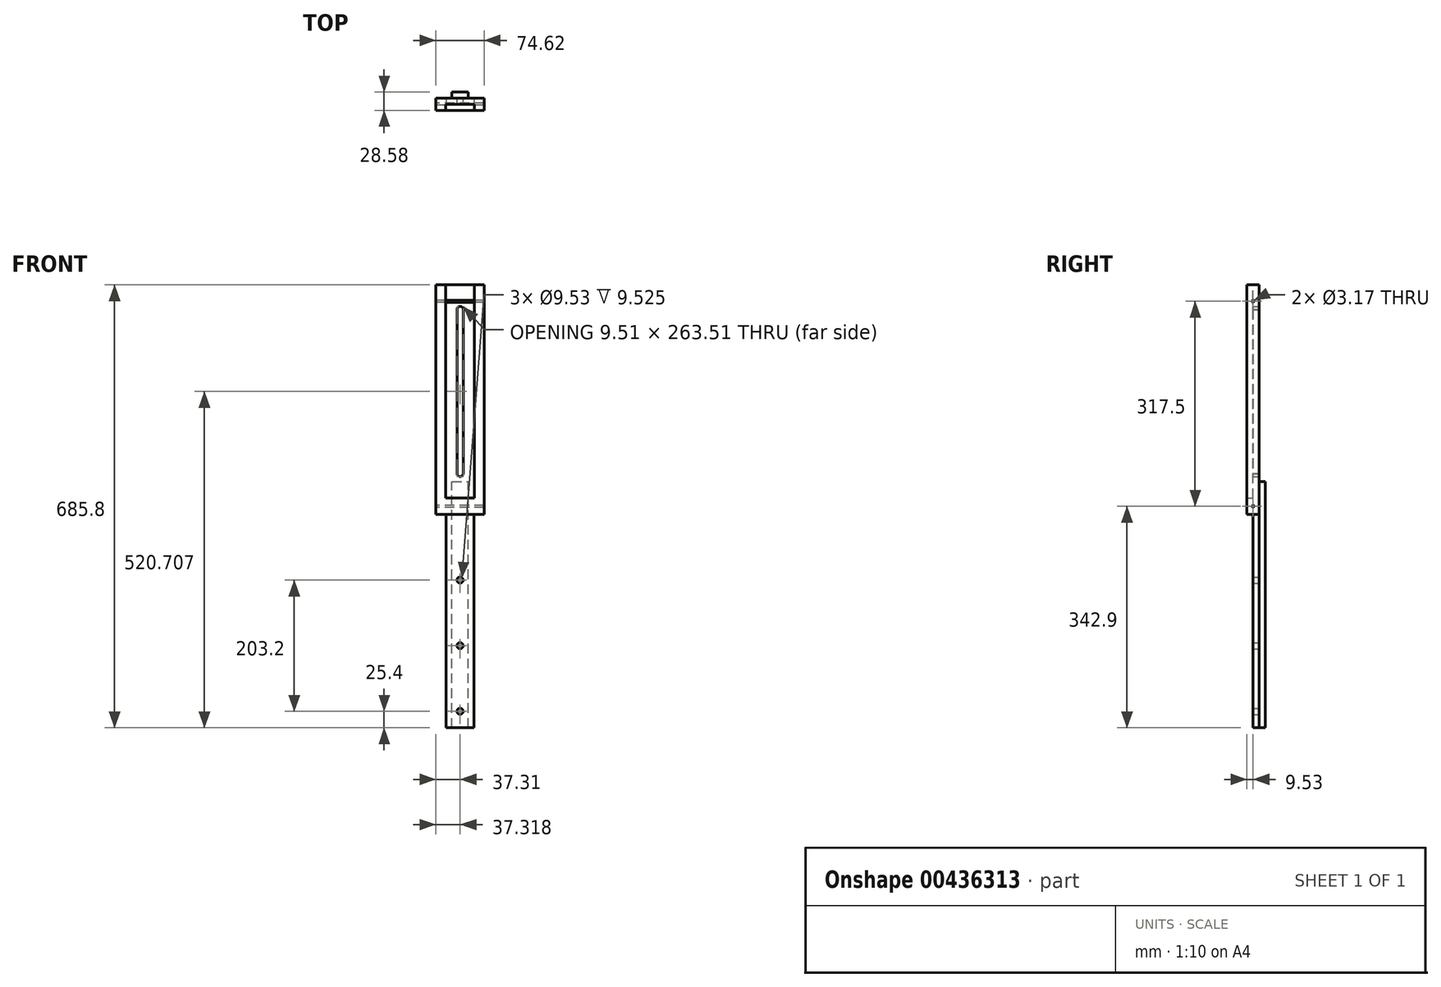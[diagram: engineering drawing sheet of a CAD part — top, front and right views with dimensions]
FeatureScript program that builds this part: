
annotation { "Feature Type Name" : "Feature", "Feature Type Description" : "" }
export const myFeature = defineFeature(function(context is Context, id is Id, definition is map)
    precondition{}
    {
        {
            var Q0;
            Q0=qCreatedBy(makeId("Top.planeOp"),FACE);
            var sketch = newSketch(context, id + "F0", { "sketchPlane" : qUnion([Q0])});
            skLineSegment(sketch, "E0.bottom", {"start": v(37.3, -9.52) * mm, "end": v(-37.3, -9.53) * mm});
            skLineSegment(sketch, "E0.top", {"start": v(37.3, 9.53) * mm, "end": v(-37.3, 9.53) * mm});
            skLineSegment(sketch, "E0.left", {"start": v(37.3, -9.52) * mm, "end": v(37.3, 9.53) * mm});
            skLineSegment(sketch, "E0.right", {"start": v(-37.3, -9.53) * mm, "end": v(-37.3, 9.53) * mm});
            skPoint(sketch, "E0.middle", {"position": v(0, 0) * mm});
            skSolve(sketch);
        }
        {
            var Q0;
            Q0 = qSketchRegion(id + "F0", true);
            extrude(context, id + "F1", {"entities" : qUnion([Q0]), "endBound" : BoundingType.SYMMETRIC, "depth" : 685.8 * mm});
        }
        {
            var Q0;
            Q0=makeQuery(id+"F1.opExtrude","CAP_FACE",FACE,{"disambiguationData":[OSD([sQuery(id+"F0.wireOp",EDGE,"E0.bottom"),sQuery(id+"F0.wireOp",EDGE,"E0.top"),sQuery(id+"F0.wireOp",EDGE,"E0.left"),sQuery(id+"F0.wireOp",EDGE,"E0.right")])],"isStart":true});
            var sketch = newSketch(context, id + "F2", { "sketchPlane" : qUnion([Q0])});
            skLineSegment(sketch, "E1.bottom", {"start": v(-12.7, -19.05) * mm, "end": v(12.7, -19.05) * mm});
            skLineSegment(sketch, "E1.top", {"start": v(-12.7, 0) * mm, "end": v(12.7, 0) * mm});
            skLineSegment(sketch, "E1.left", {"start": v(-12.7, -19.05) * mm, "end": v(-12.7, 0) * mm});
            skLineSegment(sketch, "E1.right", {"start": v(12.7, -19.05) * mm, "end": v(12.7, 0) * mm});
            skPoint(sketch, "E1.middle", {"position": v(0, -9.52) * mm});
            skSolve(sketch);
        }
        {
            var Q0;
            Q0 = qSketchRegion(id + "F2", true);
            extrude(context, id + "F3", {"entities" : qUnion([Q0]), "operationType" : NewBodyOperationType.ADD, "oppositeDirection" : true, "depth" : 381 * mm, "offsetDistance" : 25.4 * mm});
        }
        {
            var Q0;
            Q0=makeQuery(id+"F1.opExtrude","CAP_FACE",FACE,{"disambiguationData":[OSD([sQuery(id+"F0.wireOp",EDGE,"E0.bottom"),sQuery(id+"F0.wireOp",EDGE,"E0.top"),sQuery(id+"F0.wireOp",EDGE,"E0.left"),sQuery(id+"F0.wireOp",EDGE,"E0.right")])],"isStart":false});
            var sketch = newSketch(context, id + "F4", { "sketchPlane" : qUnion([Q0])});
            skLineSegment(sketch, "E2.bottom", {"start": v(22.23, -19.05) * mm, "end": v(-22.22, -19.05) * mm});
            skLineSegment(sketch, "E2.top", {"start": v(22.23, 0) * mm, "end": v(-22.22, 0) * mm});
            skLineSegment(sketch, "E2.left", {"start": v(22.23, -19.05) * mm, "end": v(22.23, 0) * mm});
            skLineSegment(sketch, "E2.right", {"start": v(-22.22, -19.05) * mm, "end": v(-22.22, 0) * mm});
            skPoint(sketch, "E2.middle", {"position": v(0, -9.52) * mm});
            skSolve(sketch);
        }
        {
            var Q0;
            Q0 = qSketchRegion(id + "F4", true);
            extrude(context, id + "F5", {"entities" : qUnion([Q0]), "operationType" : NewBodyOperationType.REMOVE, "oppositeDirection" : true, "depth" : 330.2 * mm});
        }
        {
            var Q0;
            Q0=makeQuery(id+"F1.opExtrude","CAP_FACE",FACE,{"disambiguationData":[OSD([sQuery(id+"F0.wireOp",EDGE,"E0.bottom"),sQuery(id+"F0.wireOp",EDGE,"E0.top"),sQuery(id+"F0.wireOp",EDGE,"E0.left"),sQuery(id+"F0.wireOp",EDGE,"E0.right")])],"isStart":true});
            var sketch = newSketch(context, id + "F6", { "sketchPlane" : qUnion([Q0])});
            skLineSegment(sketch, "E3.bottom", {"start": v(-37.3, -9.53) * mm, "end": v(-21.43, -9.53) * mm});
            skLineSegment(sketch, "E3.top", {"start": v(-37.3, 9.53) * mm, "end": v(-21.43, 9.53) * mm});
            skLineSegment(sketch, "E3.left", {"start": v(-37.3, -9.53) * mm, "end": v(-37.3, 9.53) * mm});
            skLineSegment(sketch, "E3.right", {"start": v(-21.43, -9.53) * mm, "end": v(-21.43, 9.53) * mm});
            skLineSegment(sketch, "E4.bottom", {"start": v(37.3, -9.53) * mm, "end": v(21.43, -9.53) * mm});
            skLineSegment(sketch, "E4.top", {"start": v(37.3, 9.53) * mm, "end": v(21.43, 9.53) * mm});
            skLineSegment(sketch, "E4.left", {"start": v(37.3, -9.53) * mm, "end": v(37.3, 9.53) * mm});
            skLineSegment(sketch, "E4.right", {"start": v(21.43, -9.53) * mm, "end": v(21.43, 9.53) * mm});
            skLineSegment(sketch, "E5.bottom", {"start": v(37.3, -9.53) * mm, "end": v(30.96, -9.53) * mm});
            skLineSegment(sketch, "E5.top", {"start": v(37.3, 9.52) * mm, "end": v(30.96, 9.52) * mm});
            skLineSegment(sketch, "E5.left", {"start": v(37.3, -9.53) * mm, "end": v(37.3, 9.52) * mm});
            skLineSegment(sketch, "E5.right", {"start": v(30.96, -9.53) * mm, "end": v(30.96, 9.52) * mm});
            skLineSegment(sketch, "E6.bottom", {"start": v(37.3, 9.52) * mm, "end": v(37.3, 9.52) * mm});
            skLineSegment(sketch, "E6.top", {"start": v(37.3, 9.52) * mm, "end": v(37.3, 9.52) * mm});
            skLineSegment(sketch, "E6.left", {"start": v(37.3, 9.52) * mm, "end": v(37.3, 9.52) * mm});
            skLineSegment(sketch, "E6.right", {"start": v(37.3, 9.52) * mm, "end": v(37.3, 9.52) * mm});
            skLineSegment(sketch, "E7.bottom", {"start": v(-37.3, -9.53) * mm, "end": v(-30.96, -9.53) * mm});
            skLineSegment(sketch, "E7.top", {"start": v(-37.3, 9.52) * mm, "end": v(-30.96, 9.52) * mm});
            skLineSegment(sketch, "E7.left", {"start": v(-37.3, -9.53) * mm, "end": v(-37.3, 9.52) * mm});
            skLineSegment(sketch, "E7.right", {"start": v(-30.96, -9.53) * mm, "end": v(-30.96, 9.52) * mm});
            skLineSegment(sketch, "E8.0.0", {"start": v(-22.22, 0) * mm, "end": v(-22.22, 9.53) * mm});
            skLineSegment(sketch, "E8.0.1", {"start": v(-22.22, 9.53) * mm, "end": v(22.23, 9.52) * mm});
            skLineSegment(sketch, "E8.0.2", {"start": v(22.23, 9.52) * mm, "end": v(22.23, 0) * mm});
            skLineSegment(sketch, "E8.0.3", {"start": v(22.23, 0) * mm, "end": v(-22.22, 0) * mm});
            skSolve(sketch);
        }
        {
            var Q0;
            Q0 = qSketchRegion(id + "F6", true);
            extrude(context, id + "F7", {"entities" : qUnion([Q0]), "operationType" : NewBodyOperationType.REMOVE, "oppositeDirection" : true, "depth" : 330.2 * mm});
        }
        {
            var Q0;
            Q0=makeQuery(id+"F1.opExtrude","SWEPT_FACE",FACE,{"disambiguationData":[OSD([sQuery(id+"F0.wireOp",EDGE,"E0.top")])]});
            var sketch = newSketch(context, id + "F8", { "sketchPlane" : qUnion([Q0])});
            skPoint(sketch, "E9", {"position": v(0, -317.5) * mm});
            skPoint(sketch, "E10", {"position": v(0, -215.9) * mm});
            skPoint(sketch, "E11", {"position": v(0, -114.3) * mm});
            skPoint(sketch, "E12", {"position": v(0, 50.8) * mm});
            skPoint(sketch, "E13", {"position": v(0, 304.8) * mm});
            skSolve(sketch);
        }
        {
            var Q0;
            Q0=sQuery(id+"F8.wireOp",VERTEX,"E9");
            var Q1;
            Q1=sQuery(id+"F8.wireOp",VERTEX,"E10");
            var Q2;
            Q2=sQuery(id+"F8.wireOp",VERTEX,"E11");
            var Q3;
            Q3=sQuery(id+"F8.wireOp",VERTEX,"E12");
            var Q4;
            Q4=sQuery(id+"F8.wireOp",VERTEX,"E13");
            var Q5;
            Q5=makeQuery(id+"F1.opExtrude","SWEPT_BODY",BODY,{"disambiguationData":[OSD([sQuery(id+"F0.wireOp",EDGE,"E0.bottom"),sQuery(id+"F0.wireOp",EDGE,"E0.top"),sQuery(id+"F0.wireOp",EDGE,"E0.left"),sQuery(id+"F0.wireOp",EDGE,"E0.right")])]});
            hole(context, id + "F9", {"style" : HoleStyle.SIMPLE, "endStyle" : HoleEndStyle.THROUGH, "holeDiameter" : 9.52 * mm, "isTappedThrough" : true, "tappedDepth" : 12.7 * mm, "tapClearance" : 3, "locations" : qUnion([Q0, Q1, Q2, Q3, Q4]), "scope" : qUnion([Q5])});
        }
        {
            var Q0;
            Q0=makeQuery(id+"F1.opExtrude","SWEPT_FACE",FACE,{"disambiguationData":[OSD([sQuery(id+"F0.wireOp",EDGE,"E0.top")])]});
            var sketch = newSketch(context, id + "F10", { "sketchPlane" : qUnion([Q0])});
            skLineSegment(sketch, "E14.bottom", {"start": v(-4.76, 304.58) * mm, "end": v(4.75, 304.58) * mm});
            skLineSegment(sketch, "E14.top", {"start": v(-4.76, 50.42) * mm, "end": v(4.75, 50.42) * mm});
            skLineSegment(sketch, "E14.left", {"start": v(-4.76, 304.58) * mm, "end": v(-4.76, 50.42) * mm});
            skLineSegment(sketch, "E14.right", {"start": v(4.75, 304.58) * mm, "end": v(4.75, 50.42) * mm});
            skSolve(sketch);
        }
        {
            var Q0;
            Q0 = qSketchRegion(id + "F10", true);
            extrude(context, id + "F11", {"entities" : qUnion([Q0]), "operationType" : NewBodyOperationType.REMOVE, "endBound" : BoundingType.THROUGH_ALL, "oppositeDirection" : true, "depth" : 25.4 * mm});
        }
        {
            var Q0;
            Q0=makeQuery(id+"F1.opExtrude","SWEPT_FACE",FACE,{"disambiguationData":[OSD([sQuery(id+"F0.wireOp",EDGE,"E0.right")])]});
            var sketch = newSketch(context, id + "F12", { "sketchPlane" : qUnion([Q0])});
            skPoint(sketch, "E15", {"position": v(0, 317.5) * mm});
            skPoint(sketch, "E16", {"position": v(0, 0) * mm});
            skSolve(sketch);
        }
        {
            var Q0;
            Q0=sQuery(id+"F12.wireOp",VERTEX,"E15");
            var Q1;
            Q1=sQuery(id+"F12.wireOp",VERTEX,"E16");
            var Q2;
            Q2=makeQuery(id+"F1.opExtrude","SWEPT_BODY",BODY,{"disambiguationData":[OSD([sQuery(id+"F0.wireOp",EDGE,"E0.bottom"),sQuery(id+"F0.wireOp",EDGE,"E0.top"),sQuery(id+"F0.wireOp",EDGE,"E0.left"),sQuery(id+"F0.wireOp",EDGE,"E0.right")])]});
            hole(context, id + "F13", {"style" : HoleStyle.SIMPLE, "endStyle" : HoleEndStyle.THROUGH, "holeDiameter" : 3.17 * mm, "isTappedThrough" : true, "tappedDepth" : 12.7 * mm, "tapClearance" : 3, "locations" : qUnion([Q0, Q1]), "scope" : qUnion([Q2])});
        }
    });
